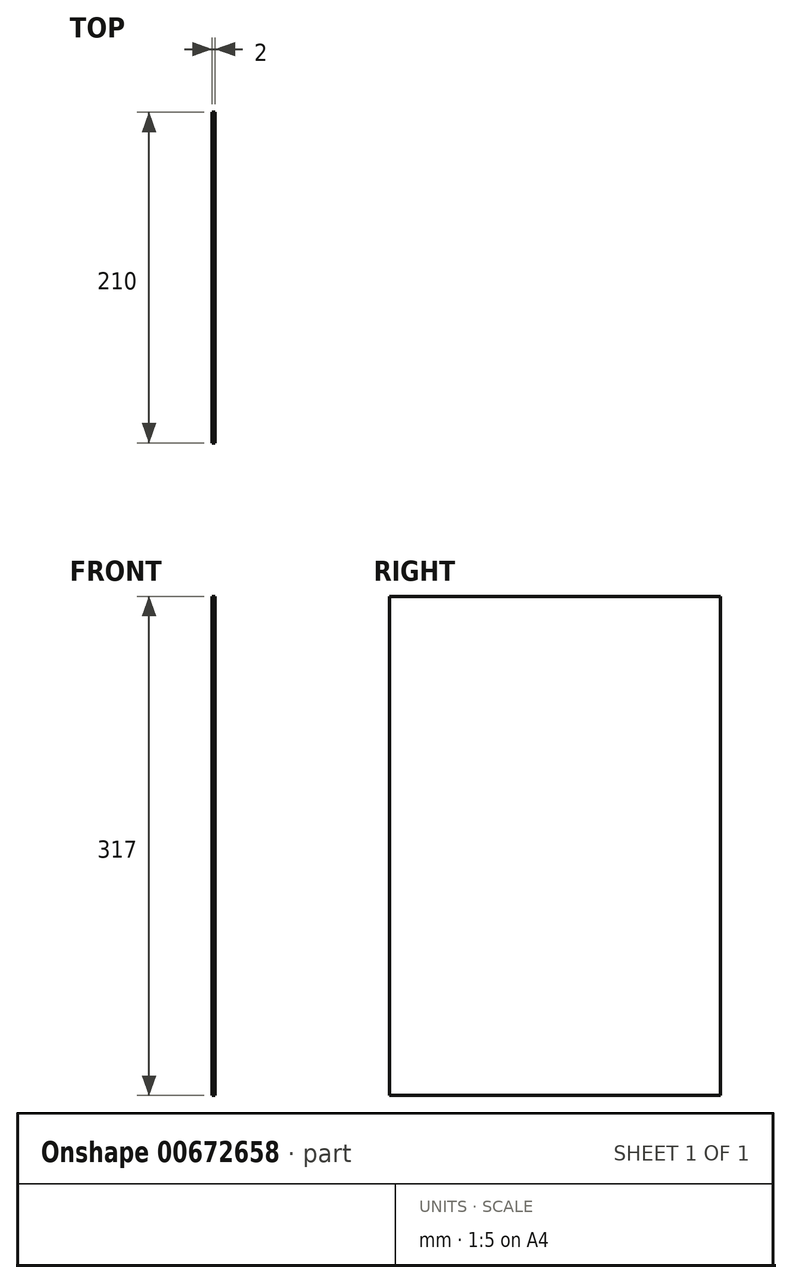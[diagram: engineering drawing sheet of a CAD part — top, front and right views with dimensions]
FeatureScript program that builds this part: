
annotation { "Feature Type Name" : "Feature", "Feature Type Description" : "" }
export const myFeature = defineFeature(function(context is Context, id is Id, definition is map)
    precondition{}
    {
        {
            var Q0;
            Q0=qCreatedBy(makeId("Right.planeOp"),FACE);
            var sketch = newSketch(context, id + "F0", { "sketchPlane" : qUnion([Q0])});
            skLineSegment(sketch, "E0.bottom", {"start": v(0, 0) * mm, "end": v(210, 0) * mm});
            skLineSegment(sketch, "E0.top", {"start": v(0, 317) * mm, "end": v(210, 317) * mm});
            skLineSegment(sketch, "E0.left", {"start": v(0, 0) * mm, "end": v(0, 317) * mm});
            skLineSegment(sketch, "E0.right", {"start": v(210, 0) * mm, "end": v(210, 317) * mm});
            skSolve(sketch);
        }
        {
            var Q0;
            Q0 = qSketchRegion(id + "F0", true);
            extrude(context, id + "F1", {"entities" : qUnion([Q0]), "depth" : 2 * mm, "offsetDistance" : 25 * mm});
        }
    });
